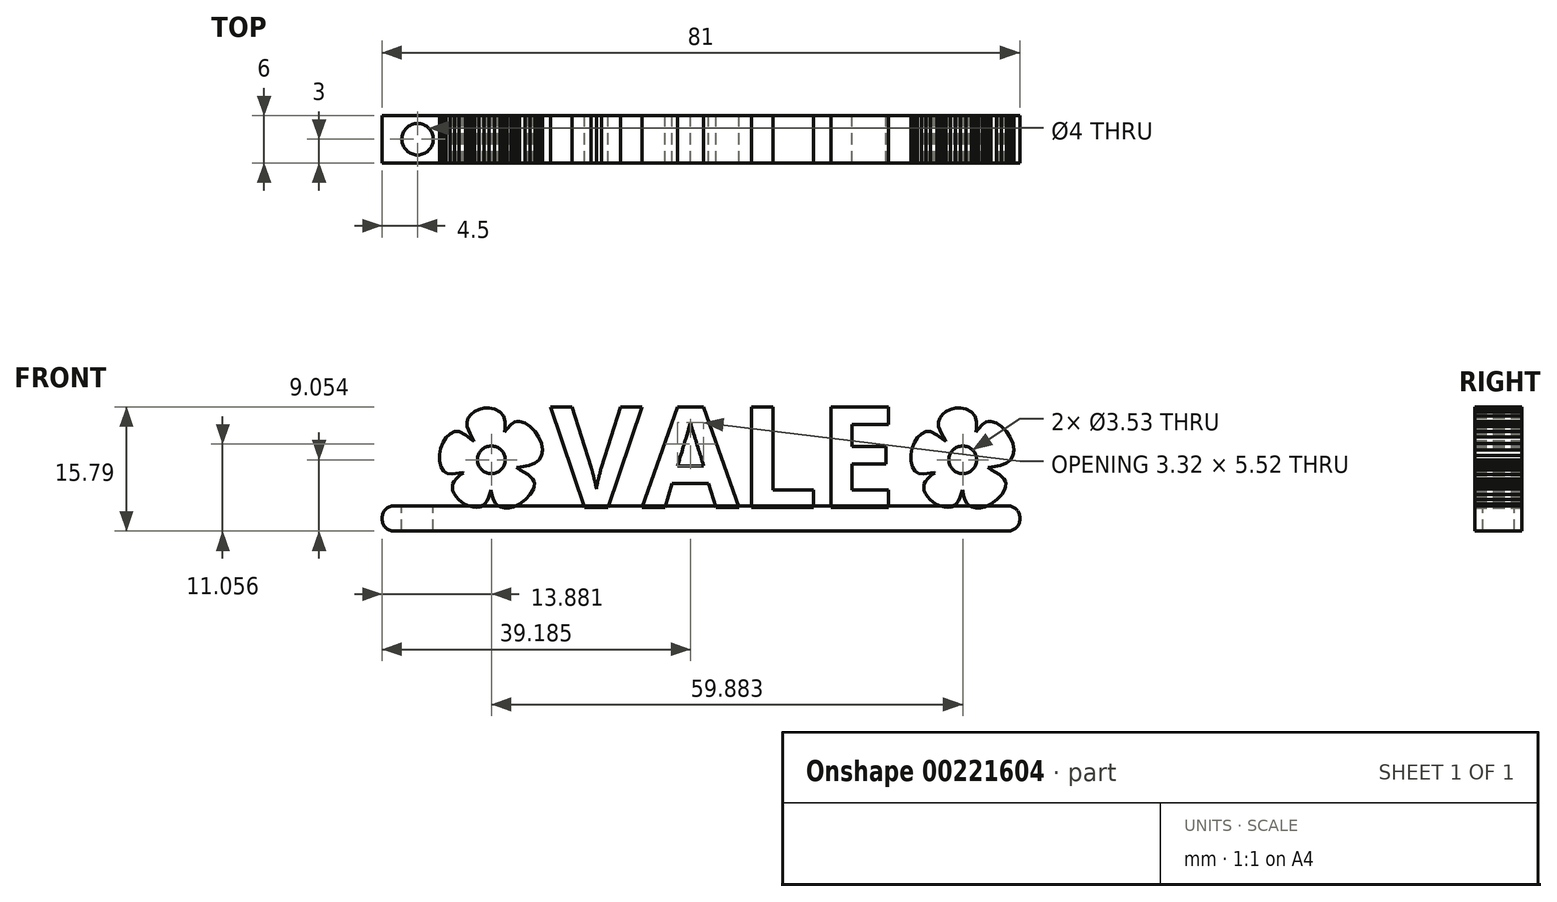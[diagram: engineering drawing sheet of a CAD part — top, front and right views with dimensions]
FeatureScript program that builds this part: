
annotation { "Feature Type Name" : "Feature", "Feature Type Description" : "" }
export const myFeature = defineFeature(function(context is Context, id is Id, definition is map)
    precondition{}
    {
        {
            var Q0;
            Q0=qCreatedBy(makeId("Front.planeOp"),FACE);
            var sketch = newSketch(context, id + "F0", { "sketchPlane" : qUnion([Q0])});
            skText(sketch, "E0", { "text": "   VALE", "fontName": "OpenSans-Bold.ttf"});
            skLineSegment(sketch, "E1.0.0", {"start": v(-9.3, 0.1) * mm, "end": v(-8.53, 0.46) * mm});
            skLineSegment(sketch, "E1.0.1", {"start": v(-8.53, 0.46) * mm, "end": v(-7.79, 1.02) * mm});
            skLineSegment(sketch, "E1.0.2", {"start": v(-7.79, 1.02) * mm, "end": v(-7.18, 1.67) * mm});
            skLineSegment(sketch, "E1.0.3", {"start": v(-7.18, 1.67) * mm, "end": v(-6.78, 2.35) * mm});
            skLineSegment(sketch, "E1.0.4", {"start": v(-6.78, 2.35) * mm, "end": v(-6.68, 2.7) * mm});
            skLineSegment(sketch, "E1.0.5", {"start": v(-6.68, 2.7) * mm, "end": v(-6.67, 3.02) * mm});
            skLineSegment(sketch, "E1.0.6", {"start": v(-6.67, 3.02) * mm, "end": v(-6.73, 3.33) * mm});
            skLineSegment(sketch, "E1.0.7", {"start": v(-6.73, 3.33) * mm, "end": v(-6.89, 3.62) * mm});
            skLineSegment(sketch, "E1.0.8", {"start": v(-6.89, 3.62) * mm, "end": v(-7.48, 4.2) * mm});
            skLineSegment(sketch, "E1.0.9", {"start": v(-7.48, 4.2) * mm, "end": v(-8.5, 4.79) * mm});
            skLineSegment(sketch, "E1.0.10", {"start": v(-8.5, 4.79) * mm, "end": v(-8.93, 5.06) * mm});
            skLineSegment(sketch, "E1.0.11", {"start": v(-8.93, 5.06) * mm, "end": v(-8.42, 5.16) * mm});
            skLineSegment(sketch, "E1.0.12", {"start": v(-8.42, 5.16) * mm, "end": v(-7.31, 5.37) * mm});
            skLineSegment(sketch, "E1.0.13", {"start": v(-7.31, 5.37) * mm, "end": v(-6.55, 5.65) * mm});
            skLineSegment(sketch, "E1.0.14", {"start": v(-6.55, 5.65) * mm, "end": v(-6.05, 6.04) * mm});
            skLineSegment(sketch, "E1.0.15", {"start": v(-6.05, 6.04) * mm, "end": v(-5.76, 6.58) * mm});
            skLineSegment(sketch, "E1.0.16", {"start": v(-5.76, 6.58) * mm, "end": v(-5.64, 7.33) * mm});
            skLineSegment(sketch, "E1.0.17", {"start": v(-5.64, 7.33) * mm, "end": v(-5.78, 8.14) * mm});
            skLineSegment(sketch, "E1.0.18", {"start": v(-5.78, 8.14) * mm, "end": v(-6.1, 8.93) * mm});
            skLineSegment(sketch, "E1.0.19", {"start": v(-6.1, 8.93) * mm, "end": v(-6.6, 9.67) * mm});
            skLineSegment(sketch, "E1.0.20", {"start": v(-6.6, 9.67) * mm, "end": v(-7.2, 10.28) * mm});
            skLineSegment(sketch, "E1.0.21", {"start": v(-7.2, 10.28) * mm, "end": v(-7.86, 10.72) * mm});
            skLineSegment(sketch, "E1.0.22", {"start": v(-7.86, 10.72) * mm, "end": v(-8.55, 10.93) * mm});
            skLineSegment(sketch, "E1.0.23", {"start": v(-8.55, 10.93) * mm, "end": v(-8.88, 10.93) * mm});
            skLineSegment(sketch, "E1.0.24", {"start": v(-8.88, 10.93) * mm, "end": v(-9.2, 10.85) * mm});
            skLineSegment(sketch, "E1.0.25", {"start": v(-9.2, 10.85) * mm, "end": v(-9.65, 10.56) * mm});
            skLineSegment(sketch, "E1.0.26", {"start": v(-9.65, 10.56) * mm, "end": v(-10.14, 9.98) * mm});
            skLineSegment(sketch, "E1.0.27", {"start": v(-10.14, 9.98) * mm, "end": v(-10.45, 9.58) * mm});
            skLineSegment(sketch, "E1.0.28", {"start": v(-10.45, 9.58) * mm, "end": v(-10.4, 10.03) * mm});
            skLineSegment(sketch, "E1.0.29", {"start": v(-10.4, 10.03) * mm, "end": v(-10.4, 10.93) * mm});
            skLineSegment(sketch, "E1.0.30", {"start": v(-10.4, 10.93) * mm, "end": v(-10.6, 11.63) * mm});
            skLineSegment(sketch, "E1.0.31", {"start": v(-10.6, 11.63) * mm, "end": v(-11.04, 12.15) * mm});
            skLineSegment(sketch, "E1.0.32", {"start": v(-11.04, 12.15) * mm, "end": v(-11.71, 12.5) * mm});
            skLineSegment(sketch, "E1.0.33", {"start": v(-11.71, 12.5) * mm, "end": v(-12.4, 12.64) * mm});
            skLineSegment(sketch, "E1.0.34", {"start": v(-12.4, 12.64) * mm, "end": v(-13.07, 12.62) * mm});
            skLineSegment(sketch, "E1.0.35", {"start": v(-13.07, 12.62) * mm, "end": v(-13.7, 12.47) * mm});
            skLineSegment(sketch, "E1.0.36", {"start": v(-13.7, 12.47) * mm, "end": v(-14.26, 12.2) * mm});
            skLineSegment(sketch, "E1.0.37", {"start": v(-14.26, 12.2) * mm, "end": v(-14.72, 11.83) * mm});
            skLineSegment(sketch, "E1.0.38", {"start": v(-14.72, 11.83) * mm, "end": v(-15.05, 11.38) * mm});
            skLineSegment(sketch, "E1.0.39", {"start": v(-15.05, 11.38) * mm, "end": v(-15.22, 10.87) * mm});
            skLineSegment(sketch, "E1.0.40", {"start": v(-15.22, 10.87) * mm, "end": v(-15.2, 10.3) * mm});
            skLineSegment(sketch, "E1.0.41", {"start": v(-15.2, 10.3) * mm, "end": v(-14.83, 9.4) * mm});
            skLineSegment(sketch, "E1.0.42", {"start": v(-14.83, 9.4) * mm, "end": v(-14.35, 8.55) * mm});
            skLineSegment(sketch, "E1.0.43", {"start": v(-14.35, 8.55) * mm, "end": v(-14.3, 8.4) * mm});
            skLineSegment(sketch, "E1.0.44", {"start": v(-14.3, 8.4) * mm, "end": v(-14.48, 8.53) * mm});
            skLineSegment(sketch, "E1.0.45", {"start": v(-14.48, 8.53) * mm, "end": v(-15.4, 9.23) * mm});
            skLineSegment(sketch, "E1.0.46", {"start": v(-15.4, 9.23) * mm, "end": v(-16.22, 9.63) * mm});
            skLineSegment(sketch, "E1.0.47", {"start": v(-16.22, 9.63) * mm, "end": v(-16.8, 9.63) * mm});
            skLineSegment(sketch, "E1.0.48", {"start": v(-16.8, 9.63) * mm, "end": v(-17.36, 9.37) * mm});
            skLineSegment(sketch, "E1.0.49", {"start": v(-17.36, 9.37) * mm, "end": v(-17.85, 8.9) * mm});
            skLineSegment(sketch, "E1.0.50", {"start": v(-17.85, 8.9) * mm, "end": v(-18.26, 8.26) * mm});
            skLineSegment(sketch, "E1.0.51", {"start": v(-18.26, 8.26) * mm, "end": v(-18.56, 7.51) * mm});
            skLineSegment(sketch, "E1.0.52", {"start": v(-18.56, 7.51) * mm, "end": v(-18.72, 6.71) * mm});
            skLineSegment(sketch, "E1.0.53", {"start": v(-18.72, 6.71) * mm, "end": v(-18.72, 5.9) * mm});
            skLineSegment(sketch, "E1.0.54", {"start": v(-18.72, 5.9) * mm, "end": v(-18.52, 5.16) * mm});
            skLineSegment(sketch, "E1.0.55", {"start": v(-18.52, 5.16) * mm, "end": v(-18.2, 4.64) * mm});
            skLineSegment(sketch, "E1.0.56", {"start": v(-18.2, 4.64) * mm, "end": v(-17.75, 4.36) * mm});
            skLineSegment(sketch, "E1.0.57", {"start": v(-17.75, 4.36) * mm, "end": v(-17.1, 4.27) * mm});
            skLineSegment(sketch, "E1.0.58", {"start": v(-17.1, 4.27) * mm, "end": v(-16.21, 4.37) * mm});
            skLineSegment(sketch, "E1.0.59", {"start": v(-16.21, 4.37) * mm, "end": v(-15.7, 4.43) * mm});
            skLineSegment(sketch, "E1.0.60", {"start": v(-15.7, 4.43) * mm, "end": v(-15.67, 4.4) * mm});
            skLineSegment(sketch, "E1.0.61", {"start": v(-15.67, 4.4) * mm, "end": v(-15.78, 4.33) * mm});
            skLineSegment(sketch, "E1.0.62", {"start": v(-15.78, 4.33) * mm, "end": v(-16.17, 4.07) * mm});
            skLineSegment(sketch, "E1.0.63", {"start": v(-16.17, 4.07) * mm, "end": v(-16.55, 3.71) * mm});
            skLineSegment(sketch, "E1.0.64", {"start": v(-16.55, 3.71) * mm, "end": v(-16.87, 3.33) * mm});
            skLineSegment(sketch, "E1.0.65", {"start": v(-16.87, 3.33) * mm, "end": v(-17.04, 3) * mm});
            skLineSegment(sketch, "E1.0.66", {"start": v(-17.04, 3) * mm, "end": v(-17.08, 2.6) * mm});
            skLineSegment(sketch, "E1.0.67", {"start": v(-17.08, 2.6) * mm, "end": v(-17.02, 2.2) * mm});
            skLineSegment(sketch, "E1.0.68", {"start": v(-17.02, 2.2) * mm, "end": v(-16.87, 1.78) * mm});
            skLineSegment(sketch, "E1.0.69", {"start": v(-16.87, 1.78) * mm, "end": v(-16.62, 1.39) * mm});
            skLineSegment(sketch, "E1.0.70", {"start": v(-16.62, 1.39) * mm, "end": v(-16.3, 1.02) * mm});
            skLineSegment(sketch, "E1.0.71", {"start": v(-16.3, 1.02) * mm, "end": v(-15.9, 0.69) * mm});
            skLineSegment(sketch, "E1.0.72", {"start": v(-15.9, 0.69) * mm, "end": v(-15.45, 0.4) * mm});
            skLineSegment(sketch, "E1.0.73", {"start": v(-15.45, 0.4) * mm, "end": v(-14.95, 0.2) * mm});
            skLineSegment(sketch, "E1.0.74", {"start": v(-14.95, 0.2) * mm, "end": v(-14.44, 0.06) * mm});
            skLineSegment(sketch, "E1.0.75", {"start": v(-14.44, 0.06) * mm, "end": v(-13.98, 0.02) * mm});
            skLineSegment(sketch, "E1.0.76", {"start": v(-13.98, 0.02) * mm, "end": v(-13.58, 0.08) * mm});
            skLineSegment(sketch, "E1.0.77", {"start": v(-13.58, 0.08) * mm, "end": v(-13.23, 0.23) * mm});
            skLineSegment(sketch, "E1.0.78", {"start": v(-13.23, 0.23) * mm, "end": v(-12.92, 0.49) * mm});
            skLineSegment(sketch, "E1.0.79", {"start": v(-12.92, 0.49) * mm, "end": v(-12.67, 0.84) * mm});
            skLineSegment(sketch, "E1.0.80", {"start": v(-12.67, 0.84) * mm, "end": v(-12.46, 1.28) * mm});
            skLineSegment(sketch, "E1.0.81", {"start": v(-12.46, 1.28) * mm, "end": v(-12.3, 1.83) * mm});
            skLineSegment(sketch, "E1.0.82", {"start": v(-12.3, 1.83) * mm, "end": v(-12.19, 2.26) * mm});
            skLineSegment(sketch, "E1.0.83", {"start": v(-12.19, 2.26) * mm, "end": v(-12.13, 2.1) * mm});
            skLineSegment(sketch, "E1.0.84", {"start": v(-12.13, 2.1) * mm, "end": v(-12.01, 1.53) * mm});
            skLineSegment(sketch, "E1.0.85", {"start": v(-12.01, 1.53) * mm, "end": v(-11.82, 1) * mm});
            skLineSegment(sketch, "E1.0.86", {"start": v(-11.82, 1) * mm, "end": v(-11.6, 0.55) * mm});
            skLineSegment(sketch, "E1.0.87", {"start": v(-11.6, 0.55) * mm, "end": v(-11.35, 0.26) * mm});
            skLineSegment(sketch, "E1.0.88", {"start": v(-11.35, 0.26) * mm, "end": v(-10.95, 0.05) * mm});
            skLineSegment(sketch, "E1.0.89", {"start": v(-10.95, 0.05) * mm, "end": v(-10.46, -0.04) * mm});
            skLineSegment(sketch, "E1.0.90", {"start": v(-10.46, -0.04) * mm, "end": v(-9.9, -0.03) * mm});
            skLineSegment(sketch, "E1.0.91", {"start": v(-9.9, -0.03) * mm, "end": v(-9.3, 0.1) * mm});
            skCircle(sketch, "E2", {"center": v(-12.12, 6.05) * mm, "radius": 1.77 * mm});
            skCircle(sketch, "E3.1.0.0", {"center": v(47.76, 6.05) * mm, "radius": 1.77 * mm});
            skLineSegment(sketch, "E3.1.0.1", {"start": v(49.43, 9.58) * mm, "end": v(49.48, 10.03) * mm});
            skLineSegment(sketch, "E3.1.0.2", {"start": v(52.69, 10.28) * mm, "end": v(52.02, 10.72) * mm});
            skLineSegment(sketch, "E3.1.0.3", {"start": v(41.17, 5.9) * mm, "end": v(41.37, 5.16) * mm});
            skLineSegment(sketch, "E3.1.0.4", {"start": v(45.62, 12.2) * mm, "end": v(45.16, 11.83) * mm});
            skLineSegment(sketch, "E3.1.0.5", {"start": v(43.58, 1.02) * mm, "end": v(43.98, 0.69) * mm});
            skLineSegment(sketch, "E3.1.0.6", {"start": v(43.67, 9.63) * mm, "end": v(43.08, 9.63) * mm});
            skLineSegment(sketch, "E3.1.0.7", {"start": v(41.32, 7.51) * mm, "end": v(41.16, 6.71) * mm});
            skLineSegment(sketch, "E3.1.0.8", {"start": v(44.49, 9.23) * mm, "end": v(43.67, 9.63) * mm});
            skLineSegment(sketch, "E3.1.0.9", {"start": v(43.08, 9.63) * mm, "end": v(42.53, 9.37) * mm});
            skLineSegment(sketch, "E3.1.0.10", {"start": v(49.74, 9.98) * mm, "end": v(49.43, 9.58) * mm});
            skLineSegment(sketch, "E3.1.0.11", {"start": v(49.28, 11.63) * mm, "end": v(48.85, 12.15) * mm});
            skLineSegment(sketch, "E3.1.0.12", {"start": v(48.85, 12.15) * mm, "end": v(48.17, 12.5) * mm});
            skLineSegment(sketch, "E3.1.0.13", {"start": v(49.5, 10.93) * mm, "end": v(49.28, 11.63) * mm});
            skLineSegment(sketch, "E3.1.0.14", {"start": v(44.43, 0.4) * mm, "end": v(44.94, 0.2) * mm});
            skLineSegment(sketch, "E3.1.0.15", {"start": v(49.99, -0.03) * mm, "end": v(50.57, 0.1) * mm});
            skLineSegment(sketch, "E3.1.0.16", {"start": v(41.16, 6.71) * mm, "end": v(41.17, 5.9) * mm});
            skLineSegment(sketch, "E3.1.0.17", {"start": v(50.57, 0.1) * mm, "end": v(51.35, 0.46) * mm});
            skLineSegment(sketch, "E3.1.0.18", {"start": v(43.98, 0.69) * mm, "end": v(44.43, 0.4) * mm});
            skLineSegment(sketch, "E3.1.0.19", {"start": v(41.37, 5.16) * mm, "end": v(41.68, 4.64) * mm});
            skLineSegment(sketch, "E3.1.0.20", {"start": v(52.57, 5.37) * mm, "end": v(53.34, 5.65) * mm});
            skLineSegment(sketch, "E3.1.0.21", {"start": v(51.35, 0.46) * mm, "end": v(52.1, 1.02) * mm});
            skLineSegment(sketch, "E3.1.0.22", {"start": v(53.29, 9.67) * mm, "end": v(52.69, 10.28) * mm});
            skLineSegment(sketch, "E3.1.0.23", {"start": v(49.48, 10.03) * mm, "end": v(49.5, 10.93) * mm});
            skLineSegment(sketch, "E3.1.0.24", {"start": v(42.53, 9.37) * mm, "end": v(42.03, 8.9) * mm});
            skLineSegment(sketch, "E3.1.0.25", {"start": v(48.17, 12.5) * mm, "end": v(47.49, 12.64) * mm});
            skLineSegment(sketch, "E3.1.0.26", {"start": v(46.81, 12.62) * mm, "end": v(46.18, 12.47) * mm});
            skLineSegment(sketch, "E3.1.0.27", {"start": v(52.7, 1.67) * mm, "end": v(53.1, 2.35) * mm});
            skLineSegment(sketch, "E3.1.0.28", {"start": v(53.77, 8.93) * mm, "end": v(53.29, 9.67) * mm});
            skLineSegment(sketch, "E3.1.0.29", {"start": v(47.49, 12.64) * mm, "end": v(46.81, 12.62) * mm});
            skLineSegment(sketch, "E3.1.0.30", {"start": v(52.1, 1.02) * mm, "end": v(52.7, 1.67) * mm});
            skLineSegment(sketch, "E3.1.0.31", {"start": v(42.03, 8.9) * mm, "end": v(41.62, 8.26) * mm});
            skLineSegment(sketch, "E3.1.0.32", {"start": v(41.62, 8.26) * mm, "end": v(41.32, 7.51) * mm});
            skLineSegment(sketch, "E3.1.0.33", {"start": v(46.18, 12.47) * mm, "end": v(45.62, 12.2) * mm});
            skLineSegment(sketch, "E3.1.0.34", {"start": v(53.1, 2.35) * mm, "end": v(53.2, 2.7) * mm});
            skLineSegment(sketch, "E3.1.0.35", {"start": v(43.08, 9.63) * mm, "end": v(42.53, 9.37) * mm});
            skLineSegment(sketch, "E3.1.0.36", {"start": v(47.49, 12.64) * mm, "end": v(46.81, 12.62) * mm});
            skLineSegment(sketch, "E3.1.0.37", {"start": v(52.57, 5.37) * mm, "end": v(53.34, 5.65) * mm});
            skLineSegment(sketch, "E3.1.0.38", {"start": v(48.93, 0.05) * mm, "end": v(49.43, -0.04) * mm});
            skLineSegment(sketch, "E3.1.0.39", {"start": v(53.77, 8.93) * mm, "end": v(53.29, 9.67) * mm});
            skLineSegment(sketch, "E3.1.0.40", {"start": v(49.99, -0.03) * mm, "end": v(50.57, 0.1) * mm});
            skLineSegment(sketch, "E3.1.0.41", {"start": v(49.74, 9.98) * mm, "end": v(49.43, 9.58) * mm});
            skLineSegment(sketch, "E3.1.0.42", {"start": v(52.1, 1.02) * mm, "end": v(52.7, 1.67) * mm});
            skLineSegment(sketch, "E3.1.0.43", {"start": v(53.1, 2.35) * mm, "end": v(53.2, 2.7) * mm});
            skLineSegment(sketch, "E3.1.0.44", {"start": v(41.16, 6.71) * mm, "end": v(41.17, 5.9) * mm});
            skLineSegment(sketch, "E3.1.0.45", {"start": v(50.57, 0.1) * mm, "end": v(51.35, 0.46) * mm});
            skLineSegment(sketch, "E3.1.0.46", {"start": v(46.81, 12.62) * mm, "end": v(46.18, 12.47) * mm});
            skLineSegment(sketch, "E3.1.0.47", {"start": v(45.62, 12.2) * mm, "end": v(45.16, 11.83) * mm});
            skLineSegment(sketch, "E3.1.0.48", {"start": v(44.43, 0.4) * mm, "end": v(44.94, 0.2) * mm});
            skLineSegment(sketch, "E3.1.0.49", {"start": v(49.48, 10.03) * mm, "end": v(49.5, 10.93) * mm});
            skLineSegment(sketch, "E3.1.0.50", {"start": v(49.43, 9.58) * mm, "end": v(49.48, 10.03) * mm});
            skLineSegment(sketch, "E3.1.0.51", {"start": v(49.43, -0.04) * mm, "end": v(49.99, -0.03) * mm});
            skLineSegment(sketch, "E3.1.0.52", {"start": v(43.67, 9.63) * mm, "end": v(43.08, 9.63) * mm});
            skLineSegment(sketch, "E3.1.0.53", {"start": v(49.5, 10.93) * mm, "end": v(49.28, 11.63) * mm});
            skLineSegment(sketch, "E3.1.0.54", {"start": v(52.69, 10.28) * mm, "end": v(52.02, 10.72) * mm});
            skLineSegment(sketch, "E3.1.0.55", {"start": v(42.03, 8.9) * mm, "end": v(41.62, 8.26) * mm});
            skLineSegment(sketch, "E3.1.0.56", {"start": v(43.98, 0.69) * mm, "end": v(44.43, 0.4) * mm});
            skLineSegment(sketch, "E3.1.0.57", {"start": v(48.17, 12.5) * mm, "end": v(47.49, 12.64) * mm});
            skLineSegment(sketch, "E3.1.0.58", {"start": v(42.53, 9.37) * mm, "end": v(42.03, 8.9) * mm});
            skLineSegment(sketch, "E3.1.0.59", {"start": v(41.17, 5.9) * mm, "end": v(41.37, 5.16) * mm});
            skLineSegment(sketch, "E3.1.0.60", {"start": v(48.85, 12.15) * mm, "end": v(48.17, 12.5) * mm});
            skLineSegment(sketch, "E3.1.0.61", {"start": v(44.49, 9.23) * mm, "end": v(43.67, 9.63) * mm});
            skLineSegment(sketch, "E3.1.0.62", {"start": v(51.35, 0.46) * mm, "end": v(52.1, 1.02) * mm});
            skLineSegment(sketch, "E3.1.0.63", {"start": v(49.28, 11.63) * mm, "end": v(48.85, 12.15) * mm});
            skLineSegment(sketch, "E3.1.0.64", {"start": v(41.62, 8.26) * mm, "end": v(41.32, 7.51) * mm});
            skLineSegment(sketch, "E3.1.0.65", {"start": v(52.7, 1.67) * mm, "end": v(53.1, 2.35) * mm});
            skLineSegment(sketch, "E3.1.0.66", {"start": v(41.32, 7.51) * mm, "end": v(41.16, 6.71) * mm});
            skLineSegment(sketch, "E3.1.0.67", {"start": v(43.58, 1.02) * mm, "end": v(43.98, 0.69) * mm});
            skLineSegment(sketch, "E3.1.0.68", {"start": v(41.37, 5.16) * mm, "end": v(41.68, 4.64) * mm});
            skLineSegment(sketch, "E3.1.0.69", {"start": v(46.18, 12.47) * mm, "end": v(45.62, 12.2) * mm});
            skLineSegment(sketch, "E3.1.0.70", {"start": v(53.29, 9.67) * mm, "end": v(52.69, 10.28) * mm});
            skLineSegment(sketch, "E3.1.0.71", {"start": v(45.16, 11.83) * mm, "end": v(44.83, 11.38) * mm});
            skLineSegment(sketch, "E3.1.0.72", {"start": v(52.02, 10.72) * mm, "end": v(51.34, 10.93) * mm});
            skLineSegment(sketch, "E3.1.0.73", {"start": v(53.83, 6.04) * mm, "end": v(54.13, 6.58) * mm});
            skLineSegment(sketch, "E3.1.0.74", {"start": v(53.2, 2.7) * mm, "end": v(53.22, 3.02) * mm});
            skLineSegment(sketch, "E3.1.0.75", {"start": v(51.34, 10.93) * mm, "end": v(51, 10.93) * mm});
            skLineSegment(sketch, "E3.1.0.76", {"start": v(41.68, 4.64) * mm, "end": v(42.13, 4.36) * mm});
            skLineSegment(sketch, "E3.1.0.77", {"start": v(50.68, 10.85) * mm, "end": v(50.24, 10.56) * mm});
            skLineSegment(sketch, "E3.1.0.78", {"start": v(51.47, 5.16) * mm, "end": v(52.57, 5.37) * mm});
            skLineSegment(sketch, "E3.1.0.79", {"start": v(53.22, 3.02) * mm, "end": v(53.15, 3.33) * mm});
            skLineSegment(sketch, "E3.1.0.80", {"start": v(53.15, 3.33) * mm, "end": v(53, 3.62) * mm});
            skLineSegment(sketch, "E3.1.0.81", {"start": v(52.4, 4.2) * mm, "end": v(51.39, 4.79) * mm});
            skLineSegment(sketch, "E3.1.0.82", {"start": v(54.24, 7.33) * mm, "end": v(54.1, 8.14) * mm});
            skLineSegment(sketch, "E3.1.0.83", {"start": v(43.26, 1.39) * mm, "end": v(43.58, 1.02) * mm});
            skLineSegment(sketch, "E3.1.0.84", {"start": v(45.44, 0.06) * mm, "end": v(45.9, 0.02) * mm});
            skLineSegment(sketch, "E3.1.0.85", {"start": v(50.96, 5.06) * mm, "end": v(51.47, 5.16) * mm});
            skLineSegment(sketch, "E3.1.0.86", {"start": v(48.53, 0.26) * mm, "end": v(48.93, 0.05) * mm});
            skLineSegment(sketch, "E3.1.0.87", {"start": v(44.83, 11.38) * mm, "end": v(44.66, 10.87) * mm});
            skLineSegment(sketch, "E3.1.0.88", {"start": v(54.13, 6.58) * mm, "end": v(54.24, 7.33) * mm});
            skLineSegment(sketch, "E3.1.0.89", {"start": v(48.93, 0.05) * mm, "end": v(49.43, -0.04) * mm});
            skLineSegment(sketch, "E3.1.0.90", {"start": v(51.39, 4.79) * mm, "end": v(50.96, 5.06) * mm});
            skLineSegment(sketch, "E3.1.0.91", {"start": v(44.94, 0.2) * mm, "end": v(45.44, 0.06) * mm});
            skLineSegment(sketch, "E3.1.0.92", {"start": v(44.69, 10.3) * mm, "end": v(45.05, 9.4) * mm});
            skLineSegment(sketch, "E3.1.0.93", {"start": v(43.02, 1.78) * mm, "end": v(43.26, 1.39) * mm});
            skLineSegment(sketch, "E3.1.0.94", {"start": v(53, 3.62) * mm, "end": v(52.4, 4.2) * mm});
            skLineSegment(sketch, "E3.1.0.95", {"start": v(49.43, -0.04) * mm, "end": v(49.99, -0.03) * mm});
            skLineSegment(sketch, "E3.1.0.96", {"start": v(44.66, 10.87) * mm, "end": v(44.69, 10.3) * mm});
            skLineSegment(sketch, "E3.1.0.97", {"start": v(53.34, 5.65) * mm, "end": v(53.83, 6.04) * mm});
            skLineSegment(sketch, "E3.1.0.98", {"start": v(51, 10.93) * mm, "end": v(50.68, 10.85) * mm});
            skLineSegment(sketch, "E3.1.0.99", {"start": v(50.24, 10.56) * mm, "end": v(49.74, 9.98) * mm});
            skLineSegment(sketch, "E3.1.0.100", {"start": v(45.9, 0.02) * mm, "end": v(46.3, 0.08) * mm});
            skLineSegment(sketch, "E3.1.0.101", {"start": v(42.86, 2.2) * mm, "end": v(43.02, 1.78) * mm});
            skLineSegment(sketch, "E3.1.0.102", {"start": v(54.1, 8.14) * mm, "end": v(53.77, 8.93) * mm});
            skLineSegment(sketch, "E3.1.0.103", {"start": v(51.39, 4.79) * mm, "end": v(50.96, 5.06) * mm});
            skLineSegment(sketch, "E3.1.0.104", {"start": v(50.96, 5.06) * mm, "end": v(51.47, 5.16) * mm});
            skLineSegment(sketch, "E3.1.0.105", {"start": v(41.68, 4.64) * mm, "end": v(42.13, 4.36) * mm});
            skLineSegment(sketch, "E3.1.0.106", {"start": v(48.29, 0.55) * mm, "end": v(48.53, 0.26) * mm});
            skLineSegment(sketch, "E3.1.0.107", {"start": v(48.53, 0.26) * mm, "end": v(48.93, 0.05) * mm});
            skLineSegment(sketch, "E3.1.0.108", {"start": v(43.02, 1.78) * mm, "end": v(43.26, 1.39) * mm});
            skLineSegment(sketch, "E3.1.0.109", {"start": v(53, 3.62) * mm, "end": v(52.4, 4.2) * mm});
            skLineSegment(sketch, "E3.1.0.110", {"start": v(51.47, 5.16) * mm, "end": v(52.57, 5.37) * mm});
            skLineSegment(sketch, "E3.1.0.111", {"start": v(44.69, 10.3) * mm, "end": v(45.05, 9.4) * mm});
            skLineSegment(sketch, "E3.1.0.112", {"start": v(53.34, 5.65) * mm, "end": v(53.83, 6.04) * mm});
            skLineSegment(sketch, "E3.1.0.113", {"start": v(50.24, 10.56) * mm, "end": v(49.74, 9.98) * mm});
            skLineSegment(sketch, "E3.1.0.114", {"start": v(54.13, 6.58) * mm, "end": v(54.24, 7.33) * mm});
            skLineSegment(sketch, "E3.1.0.115", {"start": v(44.66, 10.87) * mm, "end": v(44.69, 10.3) * mm});
            skLineSegment(sketch, "E3.1.0.116", {"start": v(51, 10.93) * mm, "end": v(50.68, 10.85) * mm});
            skLineSegment(sketch, "E3.1.0.117", {"start": v(45.9, 0.02) * mm, "end": v(46.3, 0.08) * mm});
            skLineSegment(sketch, "E3.1.0.118", {"start": v(50.68, 10.85) * mm, "end": v(50.24, 10.56) * mm});
            skLineSegment(sketch, "E3.1.0.119", {"start": v(45.44, 0.06) * mm, "end": v(45.9, 0.02) * mm});
            skLineSegment(sketch, "E3.1.0.120", {"start": v(44.94, 0.2) * mm, "end": v(45.44, 0.06) * mm});
            skLineSegment(sketch, "E3.1.0.121", {"start": v(52.4, 4.2) * mm, "end": v(51.39, 4.79) * mm});
            skLineSegment(sketch, "E3.1.0.122", {"start": v(53.83, 6.04) * mm, "end": v(54.13, 6.58) * mm});
            skLineSegment(sketch, "E3.1.0.123", {"start": v(42.8, 2.6) * mm, "end": v(42.86, 2.2) * mm});
            skLineSegment(sketch, "E3.1.0.124", {"start": v(53.2, 2.7) * mm, "end": v(53.22, 3.02) * mm});
            skLineSegment(sketch, "E3.1.0.125", {"start": v(43.26, 1.39) * mm, "end": v(43.58, 1.02) * mm});
            skLineSegment(sketch, "E3.1.0.126", {"start": v(54.1, 8.14) * mm, "end": v(53.77, 8.93) * mm});
            skLineSegment(sketch, "E3.1.0.127", {"start": v(54.24, 7.33) * mm, "end": v(54.1, 8.14) * mm});
            skLineSegment(sketch, "E3.1.0.128", {"start": v(53.22, 3.02) * mm, "end": v(53.15, 3.33) * mm});
            skLineSegment(sketch, "E3.1.0.129", {"start": v(42.86, 2.2) * mm, "end": v(43.02, 1.78) * mm});
            skLineSegment(sketch, "E3.1.0.130", {"start": v(53.15, 3.33) * mm, "end": v(53, 3.62) * mm});
            skLineSegment(sketch, "E3.1.0.131", {"start": v(44.83, 11.38) * mm, "end": v(44.66, 10.87) * mm});
            skLineSegment(sketch, "E3.1.0.132", {"start": v(51.34, 10.93) * mm, "end": v(51, 10.93) * mm});
            skLineSegment(sketch, "E3.1.0.133", {"start": v(52.02, 10.72) * mm, "end": v(51.34, 10.93) * mm});
            skLineSegment(sketch, "E3.1.0.134", {"start": v(45.16, 11.83) * mm, "end": v(44.83, 11.38) * mm});
            skLineSegment(sketch, "E3.1.0.135", {"start": v(42.8, 2.6) * mm, "end": v(42.86, 2.2) * mm});
            skLineSegment(sketch, "E3.1.0.136", {"start": v(43.67, 4.37) * mm, "end": v(44.18, 4.43) * mm});
            skLineSegment(sketch, "E3.1.0.137", {"start": v(47.87, 1.53) * mm, "end": v(48.06, 1) * mm});
            skLineSegment(sketch, "E3.1.0.138", {"start": v(44.1, 4.33) * mm, "end": v(43.72, 4.07) * mm});
            skLineSegment(sketch, "E3.1.0.139", {"start": v(46.66, 0.23) * mm, "end": v(46.96, 0.49) * mm});
            skLineSegment(sketch, "E3.1.0.140", {"start": v(47.22, 0.84) * mm, "end": v(47.42, 1.28) * mm});
            skLineSegment(sketch, "E3.1.0.141", {"start": v(48.06, 1) * mm, "end": v(48.29, 0.55) * mm});
            skLineSegment(sketch, "E3.1.0.142", {"start": v(43.72, 4.07) * mm, "end": v(43.33, 3.71) * mm});
            skLineSegment(sketch, "E3.1.0.143", {"start": v(47.75, 2.1) * mm, "end": v(47.87, 1.53) * mm});
            skLineSegment(sketch, "E3.1.0.144", {"start": v(46.96, 0.49) * mm, "end": v(47.22, 0.84) * mm});
            skLineSegment(sketch, "E3.1.0.145", {"start": v(42.77, 4.27) * mm, "end": v(43.67, 4.37) * mm});
            skLineSegment(sketch, "E3.1.0.146", {"start": v(43.33, 3.71) * mm, "end": v(43.02, 3.33) * mm});
            skLineSegment(sketch, "E3.1.0.147", {"start": v(42.13, 4.36) * mm, "end": v(42.77, 4.27) * mm});
            skLineSegment(sketch, "E3.1.0.148", {"start": v(47.42, 1.28) * mm, "end": v(47.58, 1.83) * mm});
            skLineSegment(sketch, "E3.1.0.149", {"start": v(47.7, 2.26) * mm, "end": v(47.75, 2.1) * mm});
            skLineSegment(sketch, "E3.1.0.150", {"start": v(43.02, 3.33) * mm, "end": v(42.85, 3) * mm});
            skLineSegment(sketch, "E3.1.0.151", {"start": v(48.29, 0.55) * mm, "end": v(48.53, 0.26) * mm});
            skLineSegment(sketch, "E3.1.0.152", {"start": v(47.58, 1.83) * mm, "end": v(47.7, 2.26) * mm});
            skLineSegment(sketch, "E3.1.0.153", {"start": v(42.85, 3) * mm, "end": v(42.8, 2.6) * mm});
            skLineSegment(sketch, "E3.1.0.154", {"start": v(46.3, 0.08) * mm, "end": v(46.66, 0.23) * mm});
            skLineSegment(sketch, "E3.1.0.155", {"start": v(44.21, 4.4) * mm, "end": v(44.1, 4.33) * mm});
            skLineSegment(sketch, "E3.1.0.156", {"start": v(47.7, 2.26) * mm, "end": v(47.75, 2.1) * mm});
            skLineSegment(sketch, "E3.1.0.157", {"start": v(42.77, 4.27) * mm, "end": v(43.67, 4.37) * mm});
            skLineSegment(sketch, "E3.1.0.158", {"start": v(47.87, 1.53) * mm, "end": v(48.06, 1) * mm});
            skLineSegment(sketch, "E3.1.0.159", {"start": v(44.18, 4.43) * mm, "end": v(44.21, 4.4) * mm});
            skLineSegment(sketch, "E3.1.0.160", {"start": v(43.33, 3.71) * mm, "end": v(43.02, 3.33) * mm});
            skLineSegment(sketch, "E3.1.0.161", {"start": v(42.13, 4.36) * mm, "end": v(42.77, 4.27) * mm});
            skLineSegment(sketch, "E3.1.0.162", {"start": v(43.67, 4.37) * mm, "end": v(44.18, 4.43) * mm});
            skLineSegment(sketch, "E3.1.0.163", {"start": v(46.3, 0.08) * mm, "end": v(46.66, 0.23) * mm});
            skLineSegment(sketch, "E3.1.0.164", {"start": v(43.72, 4.07) * mm, "end": v(43.33, 3.71) * mm});
            skLineSegment(sketch, "E3.1.0.165", {"start": v(47.75, 2.1) * mm, "end": v(47.87, 1.53) * mm});
            skLineSegment(sketch, "E3.1.0.166", {"start": v(47.58, 1.83) * mm, "end": v(47.7, 2.26) * mm});
            skLineSegment(sketch, "E3.1.0.167", {"start": v(44.1, 4.33) * mm, "end": v(43.72, 4.07) * mm});
            skLineSegment(sketch, "E3.1.0.168", {"start": v(46.66, 0.23) * mm, "end": v(46.96, 0.49) * mm});
            skLineSegment(sketch, "E3.1.0.169", {"start": v(42.85, 3) * mm, "end": v(42.8, 2.6) * mm});
            skLineSegment(sketch, "E3.1.0.170", {"start": v(48.06, 1) * mm, "end": v(48.29, 0.55) * mm});
            skLineSegment(sketch, "E3.1.0.171", {"start": v(46.96, 0.49) * mm, "end": v(47.22, 0.84) * mm});
            skLineSegment(sketch, "E3.1.0.172", {"start": v(47.22, 0.84) * mm, "end": v(47.42, 1.28) * mm});
            skLineSegment(sketch, "E3.1.0.173", {"start": v(43.02, 3.33) * mm, "end": v(42.85, 3) * mm});
            skLineSegment(sketch, "E3.1.0.174", {"start": v(47.42, 1.28) * mm, "end": v(47.58, 1.83) * mm});
            skLineSegment(sketch, "E3.1.0.175", {"start": v(44.21, 4.4) * mm, "end": v(44.1, 4.33) * mm});
            skLineSegment(sketch, "E3.1.0.176", {"start": v(44.18, 4.43) * mm, "end": v(44.21, 4.4) * mm});
            skLineSegment(sketch, "E3.1.0.177", {"start": v(45.6, 8.4) * mm, "end": v(45.4, 8.53) * mm});
            skLineSegment(sketch, "E3.1.0.178", {"start": v(45.53, 8.55) * mm, "end": v(45.6, 8.4) * mm});
            skLineSegment(sketch, "E3.1.0.179", {"start": v(45.05, 9.4) * mm, "end": v(45.53, 8.55) * mm});
            skLineSegment(sketch, "E3.1.0.180", {"start": v(45.4, 8.53) * mm, "end": v(44.49, 9.23) * mm});
            skLineSegment(sketch, "E3.1.0.181", {"start": v(45.53, 8.55) * mm, "end": v(45.6, 8.4) * mm});
            skLineSegment(sketch, "E3.1.0.182", {"start": v(45.05, 9.4) * mm, "end": v(45.53, 8.55) * mm});
            skLineSegment(sketch, "E3.1.0.183", {"start": v(45.4, 8.53) * mm, "end": v(44.49, 9.23) * mm});
            skLineSegment(sketch, "E3.1.0.184", {"start": v(45.6, 8.4) * mm, "end": v(45.4, 8.53) * mm});
            skLineSegment(sketch, "E3.direction1", {"start": v(-16.3, 1.02) * mm, "end": v(42.4, 1.02) * mm, "construction": true});
            const initialGuessF0  = {"E0": [-0.0185, 0, 1, 0, 0.01285]};
            skSetInitialGuess(sketch, initialGuessF0);
            skSolve(sketch);
        }
        {
            var Q0;
            Q0=qSketchRegion(id+"F0",true);
            extrude(context, id + "F1", {"entities" : qUnion([Q0]), "endBound" : BoundingType.SYMMETRIC, "depth" : 6 * mm});
        }
        {
            var Q0;
            Q0=qCreatedBy(makeId("Top.planeOp"),FACE);
            var sketch = newSketch(context, id + "F2", { "sketchPlane" : qUnion([Q0])});
            skLineSegment(sketch, "E4.bottom", {"start": v(-18.5, 3) * mm, "end": v(55, 3) * mm});
            skLineSegment(sketch, "E4.top", {"start": v(-18.5, -3) * mm, "end": v(55, -3) * mm});
            skLineSegment(sketch, "E4.left", {"start": v(-18.5, 3) * mm, "end": v(-18.5, -3) * mm});
            skLineSegment(sketch, "E4.right", {"start": v(55, 3) * mm, "end": v(55, -3) * mm});
            skSolve(sketch);
        }
        {
            var Q0;
            Q0=makeQuery(id+"F2.imprint","IMPRINT",FACE,{"disambiguationData":[TD([[makeQuery(id+"F2.imprint","IMPRINT",EDGE,{"derivedFrom":sQuery(id+"F2.wireOp",EDGE,"E4.bottom")}),-1.0]])]});
            extrude(context, id + "F3", {"entities" : qUnion([Q0]), "depth" : 0.2 * mm});
        }
        {
            var Q0;
            Q0=makeQuery(id+"F3.opExtrude","CAP_FACE",FACE,{"disambiguationData":[OSD([sQuery(id+"F2.wireOp",EDGE,"E4.bottom"),sQuery(id+"F2.wireOp",EDGE,"E4.top"),sQuery(id+"F2.wireOp",EDGE,"E4.left"),sQuery(id+"F2.wireOp",EDGE,"E4.right")])],"isStart":true});
            extrude(context, id + "F4", {"entities" : qUnion([Q0]), "depth" : 3 * mm});
        }
        {
            var Q0;
            {var subQ0=sQuery(id+"F2.wireOp",EDGE,"E4.left");Q0=makeQuery(id+"FaVoHrOpcFZXiYX_6.opBoolean","MERGE",FACE,{"derivedFrom":[makeQuery(id+"F3.opExtrude","SWEPT_FACE",FACE,{"disambiguationData":[OSD([subQ0])]}),makeQuery(id+"F4.opExtrude","SWEPT_FACE",FACE,{"disambiguationData":[OSD([subQ0])]})]});}
            var sketch = newSketch(context, id + "F5", { "sketchPlane" : qUnion([Q0])});
            skLineSegment(sketch, "E5.bottom", {"start": v(-3, -3) * mm, "end": v(3, -3) * mm});
            skLineSegment(sketch, "E5.top", {"start": v(-3, 0.2) * mm, "end": v(3, 0.2) * mm});
            skLineSegment(sketch, "E5.left", {"start": v(-3, -3) * mm, "end": v(-3, 0.2) * mm});
            skLineSegment(sketch, "E5.right", {"start": v(3, -3) * mm, "end": v(3, 0.2) * mm});
            skSolve(sketch);
        }
        {
            var Q0;
            Q0=qSketchRegion(id+"F5",true);
            extrude(context, id + "F6", {"entities" : qUnion([Q0]), "operationType" : NewBodyOperationType.ADD, "depth" : 7.5 * mm});
        }
        {
            var Q0;
            Q0=makeQuery(id+"F6.opExtrude","CAP_EDGE",EDGE,{"disambiguationData":[OSD([sQuery(id+"F5.wireOp",EDGE,"E5.bottom")])],"isStart":false});
            var Q1;
            Q1=makeQuery(id+"F6.opExtrude","CAP_EDGE",EDGE,{"disambiguationData":[OSD([sQuery(id+"F5.wireOp",EDGE,"E5.top")])],"isStart":false});
            var Q2;
            Q2=makeQuery(id+"F4.opExtrude","CAP_EDGE",EDGE,{"disambiguationData":[OSD([sQuery(id+"F2.wireOp",EDGE,"E4.right")])],"isStart":false});
            fillet(context, id + "F7", {"entities" : qUnion([Q0, Q1, Q2]), "radius" : 1.5 * mm, "tangentPropagation" : true, "allowEdgeOverflow" : false});
        }
        {
            var Q0;
            {var subQ19=sQuery(id+"F2.wireOp",EDGE,"E4.top");var subQ20=sQuery(id+"F2.wireOp",EDGE,"E4.bottom");var subQ63=sQuery(id+"F0.wireOp",EDGE,"E0.sketch_text.stroke-2");var subQ66=sQuery(id+"F2.wireOp",EDGE,"E4.left");Q0=makeQuery(id+"F6.boolean.opBoolean","MERGE",FACE,{"derivedFrom":[makeQuery(id+"FaVoHrOpcFZXiYX_6.opBoolean","SPLIT",FACE,{"disambiguationData":[TD([makeQuery(id+"F1.opExtrude","SWEPT_FACE",FACE,{"disambiguationData":[OSD([subQ63])]})])],"derivedFrom":makeQuery(id+"F3.opExtrude","CAP_FACE",FACE,{"disambiguationData":[OSD([subQ20,subQ19,subQ66,sQuery(id+"F2.wireOp",EDGE,"E4.right")])],"isStart":false})}),makeQuery(id+"F6.opExtrude","SWEPT_FACE",FACE,{"disambiguationData":[OSD([sQuery(id+"F5.wireOp",EDGE,"E5.top")])]})]});}
            var sketch = newSketch(context, id + "F8", { "sketchPlane" : qUnion([Q0])});
            skCircle(sketch, "E6", {"center": v(-21.5, 0) * mm, "radius": 2 * mm});
            skSolve(sketch);
        }
        {
            var Q0;
            Q0=makeQuery(id+"F8.imprint","IMPRINT",FACE,{"disambiguationData":[TD([[makeQuery(id+"F8.imprint","IMPRINT",EDGE,{"derivedFrom":sQuery(id+"F8.wireOp",EDGE,"E6")}),1.0]])]});
            extrude(context, id + "F9", {"entities" : qUnion([Q0]), "operationType" : NewBodyOperationType.REMOVE, "oppositeDirection" : true, "depth" : 4 * mm});
        }
        {
            var Q0;
            Q0=makeQuery(id+"F3.opExtrude","CAP_EDGE",EDGE,{"disambiguationData":[OSD([sQuery(id+"F2.wireOp",EDGE,"E4.right")])],"isStart":false});
            fillet(context, id + "F10", {"entities" : qUnion([Q0]), "radius" : 1.5 * mm, "tangentPropagation" : true, "allowEdgeOverflow" : false});
        }
    });
